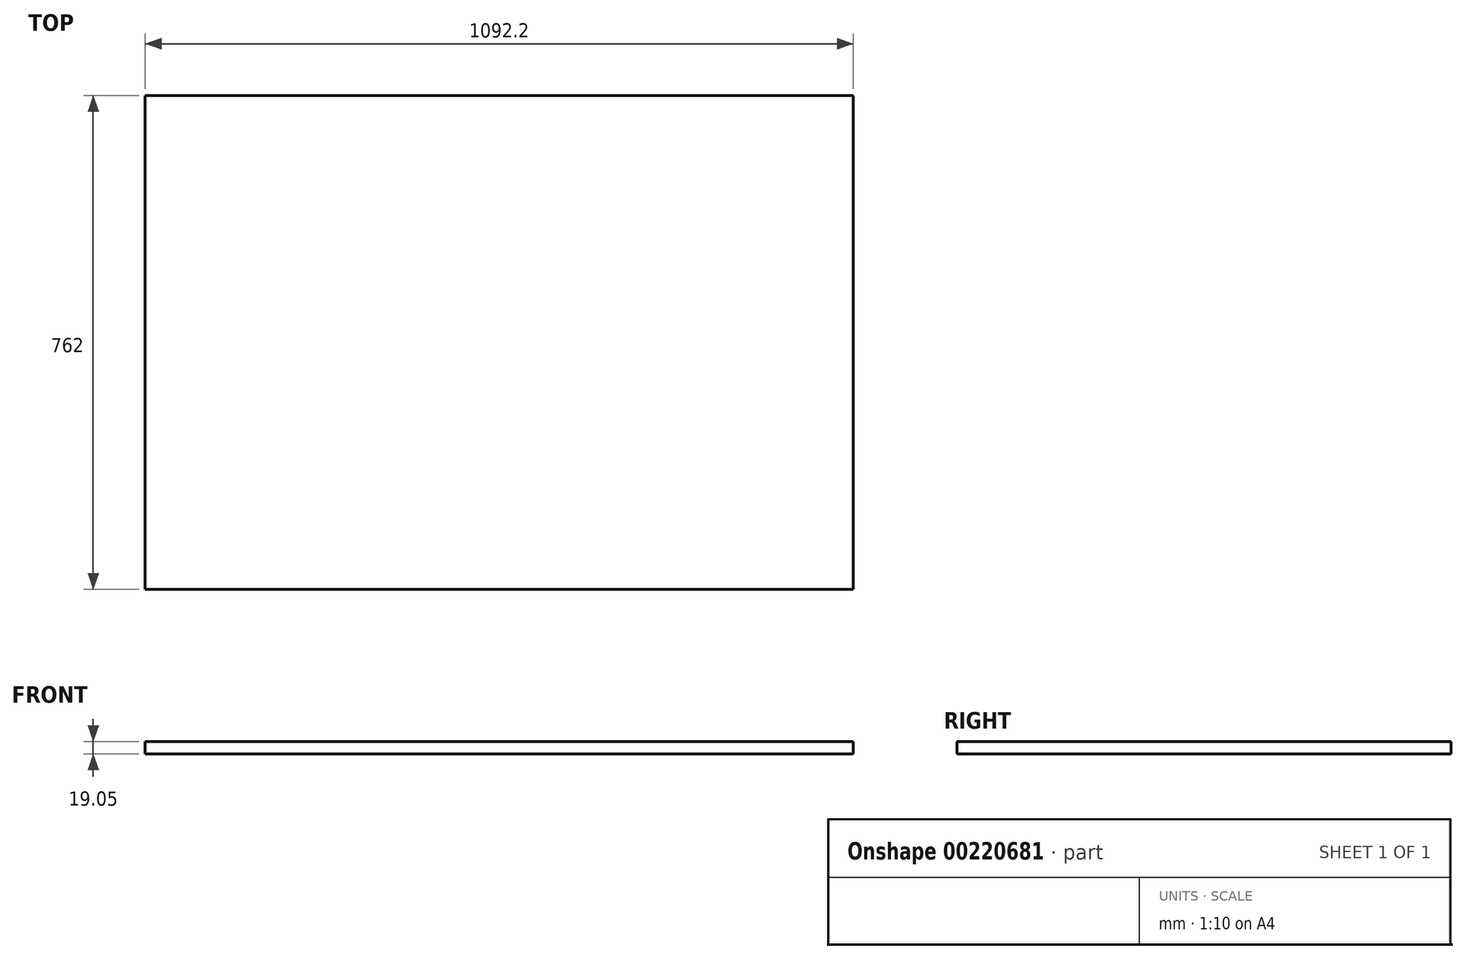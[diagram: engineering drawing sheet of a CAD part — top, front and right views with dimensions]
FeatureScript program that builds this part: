
annotation { "Feature Type Name" : "Feature", "Feature Type Description" : "" }
export const myFeature = defineFeature(function(context is Context, id is Id, definition is map)
    precondition{}
    {
        {
            var Q0;
            Q0=qCreatedBy(makeId("Top.planeOp"),FACE);
            var sketch = newSketch(context, id + "F0", { "sketchPlane" : qUnion([Q0])});
            skLineSegment(sketch, "E0.bottom", {"start": v(546.1, -381) * mm, "end": v(-546.1, -381) * mm});
            skLineSegment(sketch, "E0.top", {"start": v(546.1, 381) * mm, "end": v(-546.1, 381) * mm});
            skLineSegment(sketch, "E0.left", {"start": v(546.1, -381) * mm, "end": v(546.1, 381) * mm});
            skLineSegment(sketch, "E0.right", {"start": v(-546.1, -381) * mm, "end": v(-546.1, 381) * mm});
            skPoint(sketch, "E0.middle", {"position": v(0, 0) * mm});
            skSolve(sketch);
        }
        {
            var Q0;
            Q0 = qSketchRegion(id + "F0", true);
            extrude(context, id + "F1", {"entities" : qUnion([Q0]), "depth" : 19.05 * mm});
        }
    });
